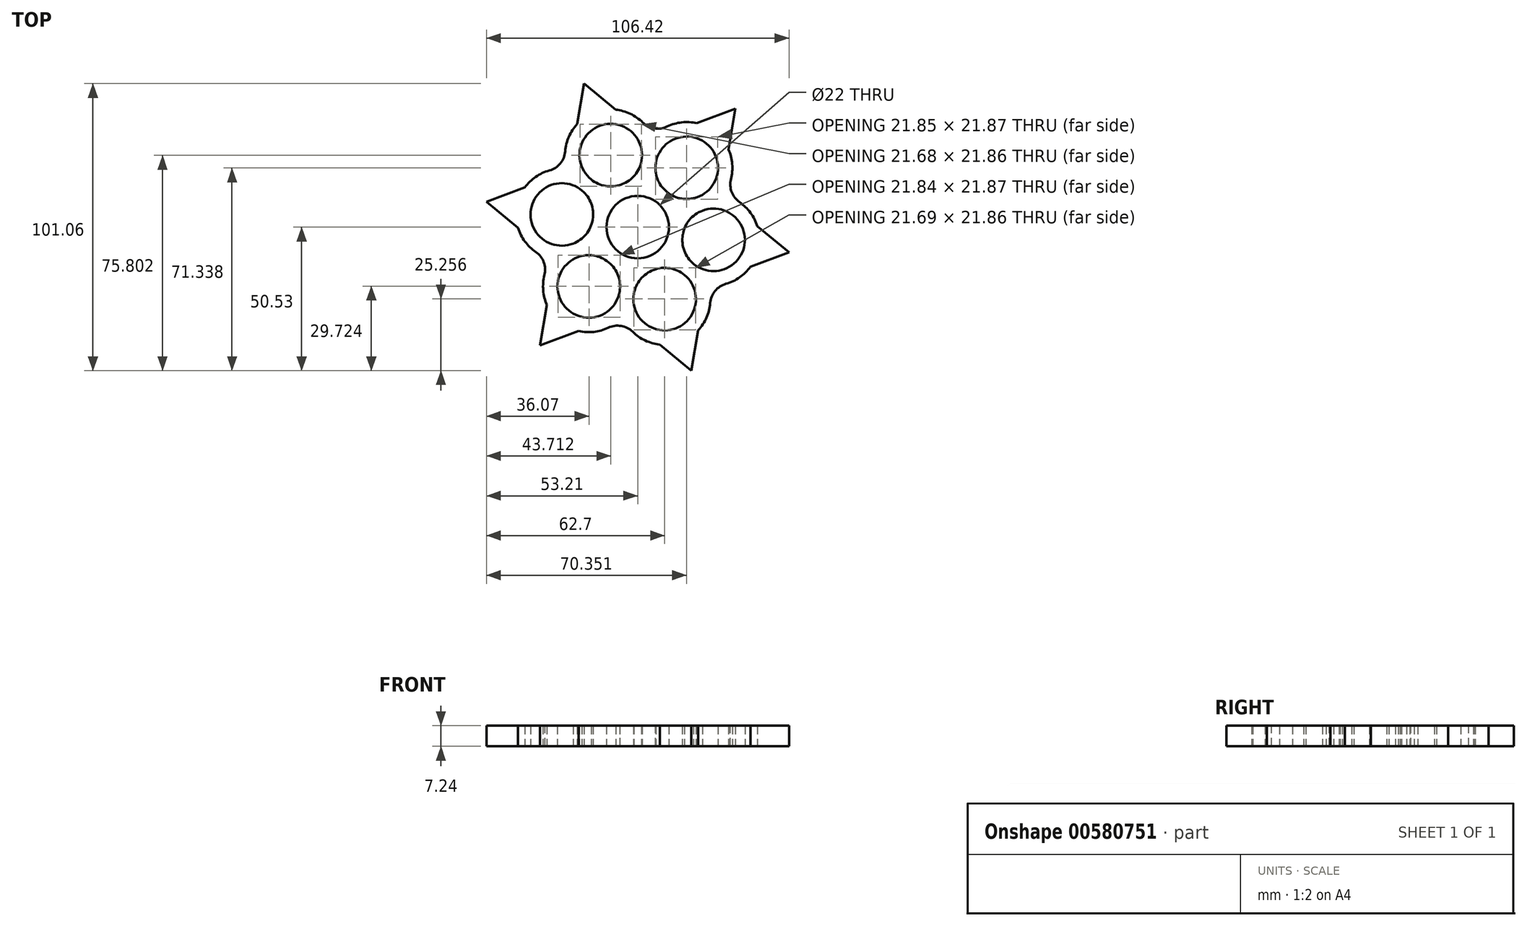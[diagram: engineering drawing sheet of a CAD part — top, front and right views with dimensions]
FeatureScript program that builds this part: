
annotation { "Feature Type Name" : "Feature", "Feature Type Description" : "" }
export const myFeature = defineFeature(function(context is Context, id is Id, definition is map)
    precondition{}
    {
        {
            var Q0;
            Q0=qCreatedBy(makeId("Top.planeOp"),FACE);
            var sketch = newSketch(context, id + "F0", { "sketchPlane" : qUnion([Q0])});
            skCircle(sketch, "E0", {"center": v(0, 0) * mm, "radius": 11 * mm});
            skCircle(sketch, "E1", {"center": v(0, 0) * mm, "radius": 16.08 * mm});
            skPoint(sketch, "E2.start.orphan", {"position": v(30.4, 0) * mm});
            skPoint(sketch, "E3.end.orphan", {"position": v(0.25, -0.44) * mm});
            skPoint(sketch, "E4.end.orphan", {"position": v(0.25, 0.15) * mm});
            skLineSegment(sketch, "E5", {"start": v(0, 0) * mm, "end": v(125.26, -20.98) * mm});
            skLineSegment(sketch, "E6", {"start": v(0, 0) * mm, "end": v(-80.8, -97.99) * mm});
            skLineSegment(sketch, "E7", {"start": v(0, 0) * mm, "end": v(-125.26, 20.98) * mm});
            skLineSegment(sketch, "E8", {"start": v(0, 0) * mm, "end": v(80.8, 97.99) * mm});
            skLineSegment(sketch, "E9", {"start": v(0, 0) * mm, "end": v(-44.46, 118.96) * mm});
            skLineSegment(sketch, "E10", {"start": v(0, 0) * mm, "end": v(44.46, -118.96) * mm});
            skSolve(sketch);
        }
        {
            var Q0;
            Q0=qCreatedBy(makeId("Top.planeOp"),FACE);
            var sketch = newSketch(context, id + "F1", { "sketchPlane" : qUnion([Q0])});
            skCircle(sketch, "E11", {"center": v(26.7, -4.47) * mm, "radius": 11 * mm});
            skPoint(sketch, "E11.first.point", {"position": v(15.86, -2.62) * mm});
            skPoint(sketch, "E11.second.point", {"position": v(37.54, -6.35) * mm});
            skPoint(sketch, "E11.third.point", {"position": v(29.44, 6.18) * mm});
            skCircle(sketch, "E12", {"center": v(26.7, -4.47) * mm, "radius": 16.08 * mm});
            skCircle(sketch, "E13", {"center": v(17.22, 20.89) * mm, "radius": 11 * mm});
            skPoint(sketch, "E13.first.point", {"position": v(10.12, 12.5) * mm});
            skPoint(sketch, "E13.second.point", {"position": v(23.84, 29.68) * mm});
            skPoint(sketch, "E13.third.point", {"position": v(26.13, 14.43) * mm});
            skCircle(sketch, "E14", {"center": v(17.22, 20.89) * mm, "radius": 16.08 * mm});
            skCircle(sketch, "E15", {"center": v(9.48, -25.36) * mm, "radius": 11 * mm});
            skPoint(sketch, "E15.first.point", {"position": v(5.5, -15.1) * mm});
            skPoint(sketch, "E15.second.point", {"position": v(12.42, -35.96) * mm});
            skPoint(sketch, "E15.third.point", {"position": v(0.14, -31.18) * mm});
            skCircle(sketch, "E16", {"center": v(-17.23, -20.9) * mm, "radius": 11 * mm});
            skPoint(sketch, "E16.first.point", {"position": v(-10.25, -12.38) * mm});
            skPoint(sketch, "E16.second.point", {"position": v(-23.9, -29.63) * mm});
            skPoint(sketch, "E16.third.point", {"position": v(-14.81, -31.62) * mm});
            skCircle(sketch, "E17", {"center": v(-26.7, 4.47) * mm, "radius": 11 * mm});
            skPoint(sketch, "E17.first.point", {"position": v(-15.88, 2.5) * mm});
            skPoint(sketch, "E17.second.point", {"position": v(-37.53, 6.39) * mm});
            skPoint(sketch, "E17.third.point", {"position": v(-28.6, -6.36) * mm});
            skCircle(sketch, "E18", {"center": v(-9.48, 25.36) * mm, "radius": 11 * mm});
            skPoint(sketch, "E18.first.point", {"position": v(-5.77, 15) * mm});
            skPoint(sketch, "E18.second.point", {"position": v(-14.63, 35.08) * mm});
            skPoint(sketch, "E18.third.point", {"position": v(-19.43, 20.68) * mm});
            skCircle(sketch, "E19", {"center": v(9.48, -25.36) * mm, "radius": 16.08 * mm});
            skCircle(sketch, "E20", {"center": v(-17.23, -20.9) * mm, "radius": 16.08 * mm});
            skCircle(sketch, "E21", {"center": v(-26.7, 4.47) * mm, "radius": 16.08 * mm});
            skCircle(sketch, "E22", {"center": v(-9.48, 25.36) * mm, "radius": 16.08 * mm});
            skLineSegment(sketch, "E23", {"start": v(-18.89, 50.53) * mm, "end": v(-21.27, 36.29) * mm});
            skLineSegment(sketch, "E24", {"start": v(-34.32, -41.62) * mm, "end": v(-20.8, -36.57) * mm});
            skLineSegment(sketch, "E25", {"start": v(53.2, -8.91) * mm, "end": v(42.07, 0.28) * mm});
            skLineSegment(sketch, "E26.trimOffspring", {"start": v(-31.94, -27.38) * mm, "end": v(-34.32, -41.62) * mm});
            skLineSegment(sketch, "E27.trimOffspring", {"start": v(-7.74, 41.35) * mm, "end": v(-18.89, 50.53) * mm});
            skLineSegment(sketch, "E28.trimOffspring", {"start": v(39.68, -13.97) * mm, "end": v(53.2, -8.91) * mm});
            skLineSegment(sketch, "E29", {"start": v(-53.2, 8.91) * mm, "end": v(-42.06, -0.28) * mm});
            skLineSegment(sketch, "E30", {"start": v(18.89, -50.53) * mm, "end": v(21.27, -36.29) * mm});
            skLineSegment(sketch, "E31", {"start": v(34.32, 41.62) * mm, "end": v(20.8, 36.57) * mm});
            skLineSegment(sketch, "E32.trimOffspring", {"start": v(-39.68, 13.97) * mm, "end": v(-53.2, 8.91) * mm});
            skLineSegment(sketch, "E33.trimOffspring", {"start": v(7.74, -41.35) * mm, "end": v(18.89, -50.53) * mm});
            skLineSegment(sketch, "E34.trimOffspring", {"start": v(31.94, 27.38) * mm, "end": v(34.32, 41.62) * mm});
            skSolve(sketch);
        }
        {
            var Q0;
            Q0 = qSketchRegion(id + "F0", true);
            extrude(context, id + "F2", {"entities" : qUnion([Q0]), "depth" : 7.24 * mm, "offsetDistance" : 25.4 * mm});
        }
        {
            var Q0;
            Q0 = qSketchRegion(id + "F1", true);
            extrude(context, id + "F3", {"entities" : qUnion([Q0]), "operationType" : NewBodyOperationType.ADD, "depth" : 7.24 * mm, "offsetDistance" : 25.4 * mm});
        }
        {
            var Q0;
            {var subQ0=sQuery(id+"F1.wireOp",EDGE,"E12");Q0=makeQuery(id+"F3.boolean.opBoolean","INTERSECT",EDGE,{"derivedFrom":[makeQuery(id+"F2.opExtrude","SWEPT_FACE",FACE,{"disambiguationData":[OSD([sQuery(id+"F0.wireOp",EDGE,"E1")])]}),makeQuery(id+"F3.opExtrude","SWEPT_FACE",FACE,{"disambiguationData":[OSD([subQ0]),TDD([makeQuery(id+"F1.imprint","IMPRINT",EDGE,{"disambiguationData":[TD([[makeQuery(id+"F1.imprint","INTERSECT",VERTEX,{"disambiguationData":[OD(1.0)],"derivedFrom":[subQ0,sQuery(id+"F1.wireOp",EDGE,"E19")]}),-1.0]])],"derivedFrom":subQ0})])]})]});}
            var Q1;
            {var subQ0=sQuery(id+"F1.wireOp",EDGE,"E20");Q1=makeQuery(id+"F3.boolean.opBoolean","INTERSECT",EDGE,{"derivedFrom":[makeQuery(id+"F2.opExtrude","SWEPT_FACE",FACE,{"disambiguationData":[OSD([sQuery(id+"F0.wireOp",EDGE,"E1")])]}),makeQuery(id+"F3.opExtrude","SWEPT_FACE",FACE,{"disambiguationData":[OSD([subQ0]),TDD([makeQuery(id+"F1.imprint","IMPRINT",EDGE,{"disambiguationData":[TD([[makeQuery(id+"F1.imprint","INTERSECT",VERTEX,{"disambiguationData":[OD(0.0)],"derivedFrom":[sQuery(id+"F1.wireOp",EDGE,"E15"),subQ0]}),-1.0]])],"derivedFrom":subQ0})])]})]});}
            var Q2;
            {var subQ0=sQuery(id+"F1.wireOp",EDGE,"E19");Q2=makeQuery(id+"F3.boolean.opBoolean","INTERSECT",EDGE,{"derivedFrom":[makeQuery(id+"F2.opExtrude","SWEPT_FACE",FACE,{"disambiguationData":[OSD([sQuery(id+"F0.wireOp",EDGE,"E1")])]}),makeQuery(id+"F3.opExtrude","SWEPT_FACE",FACE,{"disambiguationData":[OSD([subQ0]),TDD([makeQuery(id+"F1.imprint","IMPRINT",EDGE,{"disambiguationData":[TD([[makeQuery(id+"F1.imprint","INTERSECT",VERTEX,{"disambiguationData":[OD(1.0)],"derivedFrom":[sQuery(id+"F1.wireOp",EDGE,"E16"),subQ0]}),1.0]])],"derivedFrom":subQ0})])]})]});}
            var Q3;
            {var subQ0=sQuery(id+"F1.wireOp",EDGE,"E21");Q3=makeQuery(id+"F3.boolean.opBoolean","INTERSECT",EDGE,{"derivedFrom":[makeQuery(id+"F2.opExtrude","SWEPT_FACE",FACE,{"disambiguationData":[OSD([sQuery(id+"F0.wireOp",EDGE,"E1")])]}),makeQuery(id+"F3.opExtrude","SWEPT_FACE",FACE,{"disambiguationData":[OSD([subQ0]),TDD([makeQuery(id+"F1.imprint","IMPRINT",EDGE,{"disambiguationData":[TD([[makeQuery(id+"F1.imprint","INTERSECT",VERTEX,{"disambiguationData":[OD(1.0)],"derivedFrom":[sQuery(id+"F1.wireOp",EDGE,"E16"),subQ0]}),-1.0]])],"derivedFrom":subQ0})])]})]});}
            var Q4;
            {var subQ0=sQuery(id+"F1.wireOp",EDGE,"E20");Q4=makeQuery(id+"F3.boolean.opBoolean","INTERSECT",EDGE,{"derivedFrom":[makeQuery(id+"F2.opExtrude","SWEPT_FACE",FACE,{"disambiguationData":[OSD([sQuery(id+"F0.wireOp",EDGE,"E1")])]}),makeQuery(id+"F3.opExtrude","SWEPT_FACE",FACE,{"disambiguationData":[OSD([subQ0]),TDD([makeQuery(id+"F1.imprint","IMPRINT",EDGE,{"disambiguationData":[TD([[makeQuery(id+"F1.imprint","INTERSECT",VERTEX,{"disambiguationData":[OD(1.0)],"derivedFrom":[sQuery(id+"F1.wireOp",EDGE,"E17"),subQ0]}),1.0]])],"derivedFrom":subQ0})])]})]});}
            var Q5;
            {var subQ0=sQuery(id+"F1.wireOp",EDGE,"E22");Q5=makeQuery(id+"F3.boolean.opBoolean","INTERSECT",EDGE,{"derivedFrom":[makeQuery(id+"F2.opExtrude","SWEPT_FACE",FACE,{"disambiguationData":[OSD([sQuery(id+"F0.wireOp",EDGE,"E1")])]}),makeQuery(id+"F3.opExtrude","SWEPT_FACE",FACE,{"disambiguationData":[OSD([subQ0]),TDD([makeQuery(id+"F1.imprint","IMPRINT",EDGE,{"disambiguationData":[TD([[makeQuery(id+"F1.imprint","INTERSECT",VERTEX,{"disambiguationData":[OD(1.0)],"derivedFrom":[sQuery(id+"F1.wireOp",EDGE,"E17"),subQ0]}),-1.0]])],"derivedFrom":subQ0})])]})]});}
            var Q6;
            {var subQ0=sQuery(id+"F1.wireOp",EDGE,"E14");Q6=makeQuery(id+"F3.boolean.opBoolean","INTERSECT",EDGE,{"derivedFrom":[makeQuery(id+"F2.opExtrude","SWEPT_FACE",FACE,{"disambiguationData":[OSD([sQuery(id+"F0.wireOp",EDGE,"E1")])]}),makeQuery(id+"F3.opExtrude","SWEPT_FACE",FACE,{"disambiguationData":[OSD([subQ0]),TDD([makeQuery(id+"F1.imprint","IMPRINT",EDGE,{"disambiguationData":[TD([[makeQuery(id+"F1.imprint","INTERSECT",VERTEX,{"disambiguationData":[OD(1.0)],"derivedFrom":[subQ0,sQuery(id+"F1.wireOp",EDGE,"E18")]}),-1.0]])],"derivedFrom":subQ0})])]})]});}
            var Q7;
            {var subQ0=sQuery(id+"F1.wireOp",EDGE,"E21");Q7=makeQuery(id+"F3.boolean.opBoolean","INTERSECT",EDGE,{"derivedFrom":[makeQuery(id+"F2.opExtrude","SWEPT_FACE",FACE,{"disambiguationData":[OSD([sQuery(id+"F0.wireOp",EDGE,"E1")])]}),makeQuery(id+"F3.opExtrude","SWEPT_FACE",FACE,{"disambiguationData":[OSD([subQ0]),TDD([makeQuery(id+"F1.imprint","IMPRINT",EDGE,{"disambiguationData":[TD([[makeQuery(id+"F1.imprint","INTERSECT",VERTEX,{"disambiguationData":[OD(0.0)],"derivedFrom":[sQuery(id+"F1.wireOp",EDGE,"E18"),subQ0]}),1.0]])],"derivedFrom":subQ0})])]})]});}
            var Q8;
            {var subQ0=sQuery(id+"F1.wireOp",EDGE,"E12");Q8=makeQuery(id+"F3.boolean.opBoolean","INTERSECT",EDGE,{"derivedFrom":[makeQuery(id+"F2.opExtrude","SWEPT_FACE",FACE,{"disambiguationData":[OSD([sQuery(id+"F0.wireOp",EDGE,"E1")])]}),makeQuery(id+"F3.opExtrude","SWEPT_FACE",FACE,{"disambiguationData":[OSD([subQ0]),TDD([makeQuery(id+"F1.imprint","IMPRINT",EDGE,{"disambiguationData":[TD([[makeQuery(id+"F1.imprint","INTERSECT",VERTEX,{"disambiguationData":[OD(1.0)],"derivedFrom":[subQ0,sQuery(id+"F1.wireOp",EDGE,"E13")]}),-1.0]])],"derivedFrom":subQ0})])]})]});}
            var Q9;
            {var subQ0=sQuery(id+"F1.wireOp",EDGE,"E22");Q9=makeQuery(id+"F3.boolean.opBoolean","INTERSECT",EDGE,{"derivedFrom":[makeQuery(id+"F2.opExtrude","SWEPT_FACE",FACE,{"disambiguationData":[OSD([sQuery(id+"F0.wireOp",EDGE,"E1")])]}),makeQuery(id+"F3.opExtrude","SWEPT_FACE",FACE,{"disambiguationData":[OSD([subQ0]),TDD([makeQuery(id+"F1.imprint","IMPRINT",EDGE,{"disambiguationData":[TD([[makeQuery(id+"F1.imprint","INTERSECT",VERTEX,{"disambiguationData":[OD(0.0)],"derivedFrom":[sQuery(id+"F1.wireOp",EDGE,"E13"),subQ0]}),1.0]])],"derivedFrom":subQ0})])]})]});}
            var Q10;
            {var subQ0=sQuery(id+"F1.wireOp",EDGE,"E14");Q10=makeQuery(id+"F3.boolean.opBoolean","INTERSECT",EDGE,{"derivedFrom":[makeQuery(id+"F2.opExtrude","SWEPT_FACE",FACE,{"disambiguationData":[OSD([sQuery(id+"F0.wireOp",EDGE,"E1")])]}),makeQuery(id+"F3.opExtrude","SWEPT_FACE",FACE,{"disambiguationData":[OSD([subQ0]),TDD([makeQuery(id+"F1.imprint","IMPRINT",EDGE,{"disambiguationData":[TD([[makeQuery(id+"F1.imprint","INTERSECT",VERTEX,{"disambiguationData":[OD(0.0)],"derivedFrom":[sQuery(id+"F1.wireOp",EDGE,"E11"),subQ0]}),1.0]])],"derivedFrom":subQ0})])]})]});}
            var Q11;
            {var subQ0=sQuery(id+"F1.wireOp",EDGE,"E19");Q11=makeQuery(id+"F3.boolean.opBoolean","INTERSECT",EDGE,{"derivedFrom":[makeQuery(id+"F2.opExtrude","SWEPT_FACE",FACE,{"disambiguationData":[OSD([sQuery(id+"F0.wireOp",EDGE,"E1")])]}),makeQuery(id+"F3.opExtrude","SWEPT_FACE",FACE,{"disambiguationData":[OSD([subQ0]),TDD([makeQuery(id+"F1.imprint","IMPRINT",EDGE,{"disambiguationData":[TD([[makeQuery(id+"F1.imprint","INTERSECT",VERTEX,{"disambiguationData":[OD(0.0)],"derivedFrom":[sQuery(id+"F1.wireOp",EDGE,"E11"),subQ0]}),-1.0]])],"derivedFrom":subQ0})])]})]});}
            fillet(context, id + "F4", {"entities" : qUnion([Q0, Q1, Q2, Q3, Q4, Q5, Q6, Q7, Q8, Q9, Q10, Q11]), "radius" : 10.8 * mm, "tangentPropagation" : true, "allowEdgeOverflow" : false});
        }
        {
            var Q0;
            {var subQ0=sQuery(id+"F1.wireOp",EDGE,"E19");var subQ1=sQuery(id+"F1.wireOp",EDGE,"E12");Q0=makeQuery(id+"F3.opExtrude","SWEPT_EDGE",EDGE,{"disambiguationData":[OSD([subQ1,subQ0]),TDD([makeQuery(id+"F1.imprint","INTERSECT",VERTEX,{"disambiguationData":[OD(0.0)],"derivedFrom":[subQ1,subQ0]})])]});}
            var Q1;
            {var subQ0=sQuery(id+"F1.wireOp",EDGE,"E20");var subQ1=sQuery(id+"F1.wireOp",EDGE,"E19");Q1=makeQuery(id+"F3.opExtrude","SWEPT_EDGE",EDGE,{"disambiguationData":[OSD([subQ1,subQ0]),TDD([makeQuery(id+"F1.imprint","INTERSECT",VERTEX,{"disambiguationData":[OD(0.0)],"derivedFrom":[subQ1,subQ0]})])]});}
            var Q2;
            {var subQ0=sQuery(id+"F1.wireOp",EDGE,"E21");var subQ1=sQuery(id+"F1.wireOp",EDGE,"E20");Q2=makeQuery(id+"F3.opExtrude","SWEPT_EDGE",EDGE,{"disambiguationData":[OSD([subQ1,subQ0]),TDD([makeQuery(id+"F1.imprint","INTERSECT",VERTEX,{"disambiguationData":[OD(0.0)],"derivedFrom":[subQ1,subQ0]})])]});}
            var Q3;
            {var subQ0=sQuery(id+"F1.wireOp",EDGE,"E22");var subQ1=sQuery(id+"F1.wireOp",EDGE,"E21");Q3=makeQuery(id+"F3.opExtrude","SWEPT_EDGE",EDGE,{"disambiguationData":[OSD([subQ1,subQ0]),TDD([makeQuery(id+"F1.imprint","INTERSECT",VERTEX,{"disambiguationData":[OD(0.0)],"derivedFrom":[subQ1,subQ0]})])]});}
            var Q4;
            {var subQ0=sQuery(id+"F1.wireOp",EDGE,"E22");var subQ1=sQuery(id+"F1.wireOp",EDGE,"E14");Q4=makeQuery(id+"F3.opExtrude","SWEPT_EDGE",EDGE,{"disambiguationData":[OSD([subQ1,subQ0]),TDD([makeQuery(id+"F1.imprint","INTERSECT",VERTEX,{"disambiguationData":[OD(0.0)],"derivedFrom":[subQ1,subQ0]})])]});}
            var Q5;
            {var subQ0=sQuery(id+"F1.wireOp",EDGE,"E14");var subQ1=sQuery(id+"F1.wireOp",EDGE,"E12");Q5=makeQuery(id+"F3.opExtrude","SWEPT_EDGE",EDGE,{"disambiguationData":[OSD([subQ1,subQ0]),TDD([makeQuery(id+"F1.imprint","INTERSECT",VERTEX,{"disambiguationData":[OD(0.0)],"derivedFrom":[subQ1,subQ0]})])]});}
            fillet(context, id + "F5", {"entities" : qUnion([Q0, Q1, Q2, Q3, Q4, Q5]), "radius" : 7.62 * mm, "tangentPropagation" : true, "allowEdgeOverflow" : false});
        }
    });
